# Revit family: Centre pivot window FAKRO FTP-V U5
name_source: partatom
category: Okna
revit_build: Autodesk Revit 2015 (Build: 20140606_1530(x64)
units: mm (PartAtom-declared; Revit-internal decimal feet)

## types (14) — shared parameters
Apron Material = Fakro - aluminium RAL7022
Bimobject Category = Windows - Roof Windows
CSI MasterFormat 2016 Code = 08 60 00
CSI MasterFormat 2016 Title = Roof Windows and Skylights
CSI UniFormat II Code = B3020
CSI UniFormat II Title = Roof Openings
Glazing = Fakro - Glass
Handle Material = Fakro - handle
IFC Classification = Window
Kod zespołu = B3020110
Material External = Fakro - aluminium RAL7022
Material Internal = Fakro - frame - pinewood
Model = FTP-V U5
NBS Reference = 59-72
NBS Reference Description = Roof Window Units
Opis = Centre pivot window
Producent = FAKRO
UNSPC Category = Roofing accessories
UNSPC Code = 301516
URL = www.fakro.com
UV radiation EN 410 = 0.28
Uniclass 1.4 Code = JL11
Uniclass 1.4 Description = Rooflights/Roof windows
Uniclass 2.0 Code = PR-59-72
Uniclass 2.0 Description = Roof Window Units
Uniclass 2015 Code = Pr_30_59_72_77
Uniclass 2015 Title = Skylights
air inlet = V40P
air permeability class EN 1026; EN 12207 = 4
colour = Natural – pine
frame thermal insulation Uf [W/m2K] EN ISO 10077-1; EN ISO 10077-2 = 1.7
glass structure = 4HT-10-4H-10-4HT
glazing U-value [W/m2K] EN 12567-2 = 0.5
impact resistance EN 13049 [class] = 3
light transmittance factor tv EN 410 = 0.73
material = pinewood
opening method = centre pivot
operation mode = manual
reaction to fire = D-s2;d2
roof angle = 15 -90
solar factor [ g] EN 410 = 0.53
thermal insulation of frame and glazing connection (psi) [W/mK] EN ISO 10077-1; EN ISO 10077-2 = 0.051
watertightness / unshielded (A) EN 12208 = E900
window acoustic performance Rw [dB] EN ISO 717-1 = 33(-2;-6)
window heat transfer coefficient Uw [W/m2K] EN 673 = 0.97

## per-type parameters (varying)
| type | Obj Type | Szerokość | Wysokość | air inlet efficiency - 10Pa | frame area | glass perimeter | glazing area | window internal area | window perimeter | window weight |
| FTP-V U5 - 01 - 55x78 | 1 mm  [stored 0.00328084 ft] | 547 mm  [stored 1.79462 ft] | 781 mm  [stored 2.56234 ft] | 17 m³/h | 0.21 m² | 1920 mm  [stored 6.29921 ft] | 0.22 m² | 0.32 m² | 2660 mm  [stored 8.72703 ft] | 21.50 kg |
| FTP-V U5 - 02 - 55x98 | 2 mm  [stored 0.00656168 ft] | 547 mm  [stored 1.79462 ft] | 981 mm  [stored 3.2185 ft] | 17 m³/h | 0.24 m² | 2320 mm | 0.29 m² | 0.41 m² | 3060 mm  [stored 10.0394 ft] | 26.50 kg |
| FTP-V U5 - 03 - 66x98 | 3 mm  [stored 0.00984252 ft] | 657 mm | 981 mm  [stored 3.2185 ft] | 23 m³/h | 0.27 m² | 2540 mm  [stored 8.33333 ft] | 0.38 m² | 0.51 m² | 3280 mm | 30.30 kg |
| FTP-V U5 - 04 - 66x118 | 4 mm  [stored 0.0131234 ft] | 657 mm | 1181 mm  [stored 3.87467 ft] | 23 m³/h | 0.3 m² | 2940 mm  [stored 9.64567 ft] | 0.47 m² | 0.62 m² | 3680 mm  [stored 12.0735 ft] | 37.20 kg |
| FTP-V U5 - 05 - 78x98 | 5 mm  [stored 0.0164042 ft] | 777 mm  [stored 2.54921 ft] | 981 mm  [stored 3.2185 ft] | 27 m³/h | 0.29 m² | 2780 mm  [stored 9.12073 ft] | 0.47 m² | 0.62 m² | 3520 mm  [stored 11.5486 ft] | 36.10 kg |
| FTP-V U5 - 06 - 78x118 | 6 mm  [stored 0.019685 ft] | 777 mm  [stored 2.54921 ft] | 1181 mm  [stored 3.87467 ft] | 27 m³/h | 0.32 m² | 3180 mm  [stored 10.4331 ft] | 0.59 m² | 0.75 m² | 3920 mm | 41.00 kg |
| FTP-V U5 - 07 - 78x140 | 7 mm  [stored 0.0229659 ft] | 777 mm  [stored 2.54921 ft] | 1401 mm | 27 m³/h | 0.36 m² | 3620 mm  [stored 11.8766 ft] | 0.73 m² | 0.91 m² | 4360 mm | 45.90 kg |
| FTP-V U5 - 08 - 94x118 | 8 mm  [stored 0.0262467 ft] | 937 mm  [stored 3.07415 ft] | 1181 mm  [stored 3.87467 ft] | 27 m³/h | 0.35 m² | 3500 mm | 0.75 m² | 0.93 m² | 4240 mm | 46.70 kg |
| FTP-V U5 - 09 - 94x140 | 9 mm  [stored 0.0295276 ft] | 937 mm  [stored 3.07415 ft] | 1401 mm | 27 m³/h | 0.43 m² | 4340 mm | 1.16 m² | 1.12 m² | 5080 mm | 55.50 kg |
| FTP-V U5 - 10 - 114x118 | 10 mm  [stored 0.0328084 ft] | 1137 mm  [stored 3.73031 ft] | 1181 mm  [stored 3.87467 ft] | 49 m³/h | 0.39 m² | 3900 mm | 0.95 m² | 1.15 m² | 4640 mm | 56.20 kg |
| FTP-V U5 - 11 - 114x140 | 11 mm  [stored 0.0360892 ft] | 1137 mm  [stored 3.73031 ft] | 1401 mm | 49 m³/h | 0.43 m² | 4340 mm | 1.16 m² | 1.38 m² | 5080 mm | 63.10 kg |
| FTP-V U5 - 12 - 134x98 | 12 mm  [stored 0.0393701 ft] | 1337 mm  [stored 4.38648 ft] | 981 mm  [stored 3.2185 ft] | 49 m³/h | 0.39 m² | 3900 mm | 0.92 m² | 1.12 m² | 4640 mm | 55.00 kg |
| FTP-V U5 - 13 - 78x160 | 13 mm  [stored 0.0426509 ft] | 777 mm  [stored 2.54921 ft] | 1601 mm  [stored 5.25262 ft] | 27 m³/h | 0.4 m² | 4020 mm | 0.85 m² | 1.05 m² | 4760 mm | 55.00 kg |
| FTP-V U5 - 14 - 66x140 | 14 mm  [stored 0.0459318 ft] | 657 mm | 1401 mm | 23 m³/h | 0.34 m² | 3560 mm  [stored 11.6798 ft] | 0.58 m² | 0.74 m² | 4120 mm | 41.20 kg |

note: [stored X ft] marks values corroborated as IEEE doubles in the binary element streams (Revit-internal decimal feet)

## geometry (parser evidence)
native form markers: Sweep x3
no freeform markers — native parametric forms only
